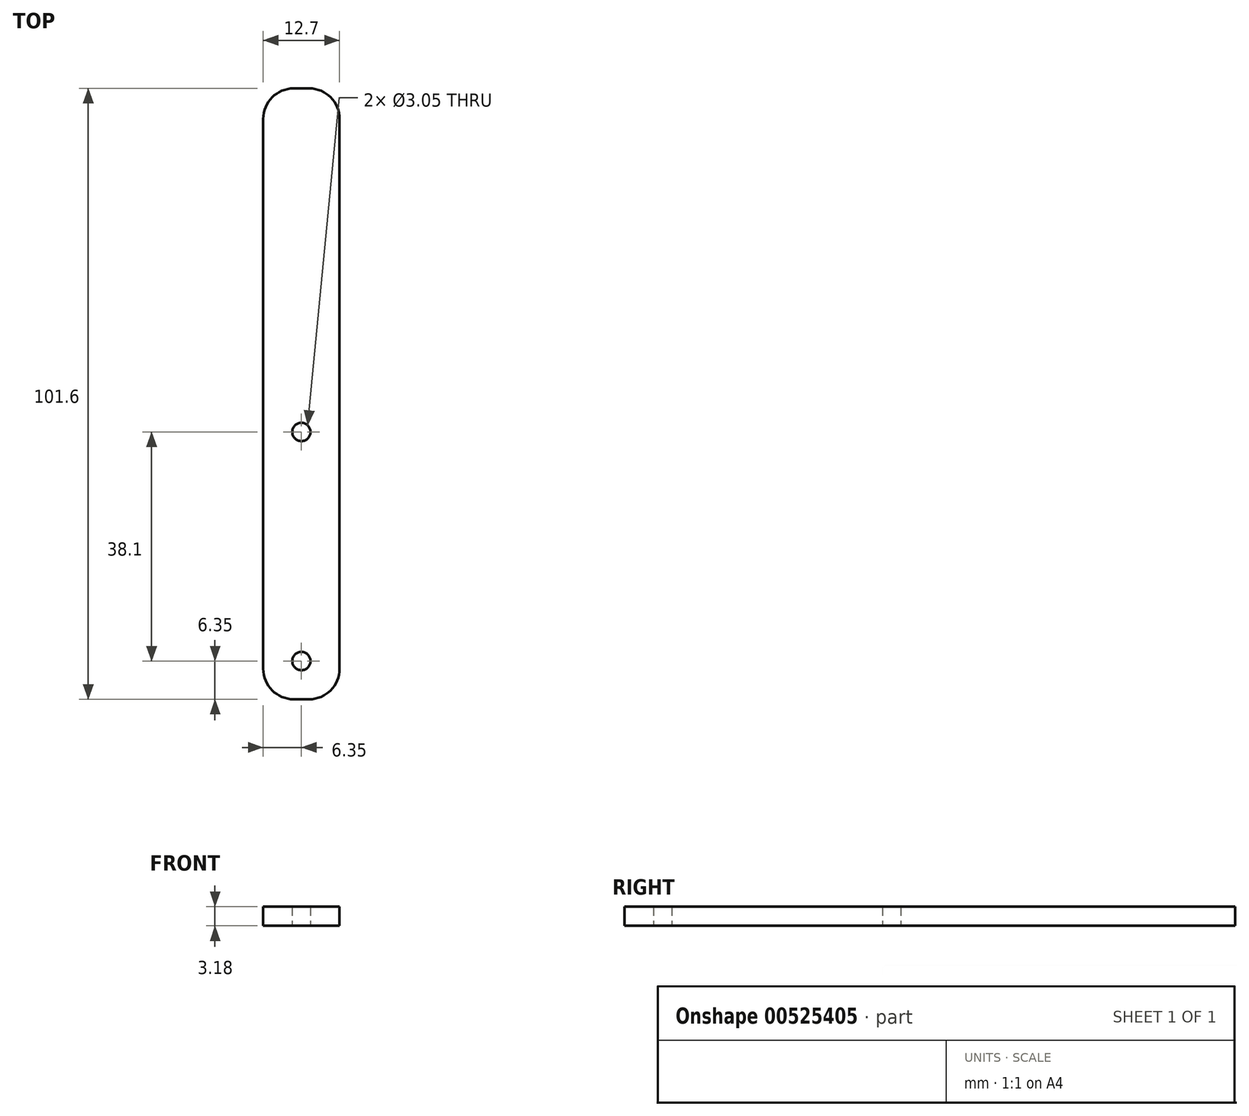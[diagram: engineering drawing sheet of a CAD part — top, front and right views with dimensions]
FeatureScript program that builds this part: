
annotation { "Feature Type Name" : "Feature", "Feature Type Description" : "" }
export const myFeature = defineFeature(function(context is Context, id is Id, definition is map)
    precondition{}
    {
        {
            var Q0;
            Q0=qCreatedBy(makeId("Top.planeOp"),FACE);
            var sketch = newSketch(context, id + "F0", { "sketchPlane" : qUnion([Q0])});
            skLineSegment(sketch, "E0.bottom", {"start": v(6.35, -25.4) * mm, "end": v(-6.35, -25.4) * mm});
            skLineSegment(sketch, "E0.left", {"start": v(6.35, -25.4) * mm, "end": v(6.35, 25.4) * mm});
            skLineSegment(sketch, "E0.right", {"start": v(-6.35, -25.4) * mm, "end": v(-6.35, 25.4) * mm});
            skPoint(sketch, "E0.middle", {"position": v(0, 0) * mm});
            skCircle(sketch, "E1", {"center": v(0, -19.05) * mm, "radius": 1.52 * mm});
            skCircle(sketch, "E2.MirrorC", {"center": v(0, 19.05) * mm, "radius": 1.52 * mm});
            skLineSegment(sketch, "E3.top", {"start": v(-6.35, 76.2) * mm, "end": v(6.35, 76.2) * mm});
            skLineSegment(sketch, "E3.left", {"start": v(-6.35, 25.4) * mm, "end": v(-6.35, 76.2) * mm});
            skLineSegment(sketch, "E3.right", {"start": v(6.35, 25.4) * mm, "end": v(6.35, 76.2) * mm});
            skSolve(sketch);
        }
        {
            var Q0;
            Q0=makeQuery(id+"F0.imprint","IMPRINT",FACE,{"disambiguationData":[TD([[makeQuery(id+"F0.imprint","IMPRINT",EDGE,{"derivedFrom":sQuery(id+"F0.wireOp",EDGE,"E0.bottom")}),-1.0]])]});
            var Q1;
            Q1=makeQuery(id+"F0.imprint","IMPRINT",FACE,{"disambiguationData":[TD([[makeQuery(id+"F0.imprint","IMPRINT",EDGE,{"derivedFrom":sQuery(id+"F0.wireOp",EDGE,"E3.bottom")}),1.0]])]});
            extrude(context, id + "F1", {"entities" : qUnion([Q0, Q1]), "depth" : 3.17 * mm, "offsetDistance" : 25.4 * mm});
        }
        {
            var Q0;
            Q0=makeQuery(id+"F1.opExtrude","SWEPT_EDGE",EDGE,{"disambiguationData":[OSD([sQuery(id+"F0.wireOp",EDGE,"E3.top"),sQuery(id+"F0.wireOp",EDGE,"E3.left")])]});
            var Q1;
            Q1=makeQuery(id+"F1.opExtrude","SWEPT_EDGE",EDGE,{"disambiguationData":[OSD([sQuery(id+"F0.wireOp",EDGE,"E3.top"),sQuery(id+"F0.wireOp",EDGE,"E3.right")])]});
            var Q2;
            Q2=makeQuery(id+"F1.opExtrude","SWEPT_EDGE",EDGE,{"disambiguationData":[OSD([sQuery(id+"F0.wireOp",EDGE,"E0.bottom"),sQuery(id+"F0.wireOp",EDGE,"E0.right")])]});
            var Q3;
            Q3=makeQuery(id+"F1.opExtrude","SWEPT_EDGE",EDGE,{"disambiguationData":[OSD([sQuery(id+"F0.wireOp",EDGE,"E0.bottom"),sQuery(id+"F0.wireOp",EDGE,"E0.left")])]});
            fillet(context, id + "F2", {"entities" : qUnion([Q0, Q1, Q2, Q3]), "radius" : 5.08 * mm, "tangentPropagation" : true, "allowEdgeOverflow" : false});
        }
    });
